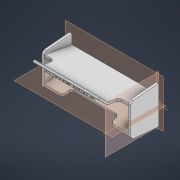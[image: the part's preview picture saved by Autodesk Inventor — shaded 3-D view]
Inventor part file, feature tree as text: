
AUTODESK INVENTOR PART (.ipt)
format: ipt  version: 2021 (Build 250183000, 183)  size: 4,402,176 bytes
history: native  units: mm
features: other x5, extrude x5, sketch x4, chamfer x2, move_body x2, fillet x1, mirror x1
ambient origin geometry x8: Origin, YZ Plane, XZ Plane, XY Plane, X Axis, Y Axis, Z Axis, Center Point
bodies: Solid1 (feature_tree)
feature tree (20):
  other  "Blocks"
  extrude  "Extrusion1"  Depth=35.0mm
  extrude  "Extrusion2"  TaperAngle=0.0deg  [1 undecoded]
  extrude  "Extrusion5"  Depth=2.5mm
  extrude  "Extrusion6"  Depth=2.5mm
  fillet  "Fillet1"  Radius=2.5mm
  mirror  "Mirror1"
  extrude  "Extrusion8"  Depth=2.5mm
  chamfer  "Chamfer1"  Distance=17.453293mm
  chamfer  "Chamfer2"  Distance=17.453293mm
  move_body  "Move Body1"
  move_body  "Move Body2"
  sketch  "Sketch2"  dims[d4=30.0mm d5=35.0mm]
  sketch  "Sketch5"  dims[d6=40.0mm d14=0.0mm]
  sketch  "Sketch8"  dims[d15=2.5mm d16=2.5mm]
  other  "Block1"
  sketch  "Sketch15"  dims[d17=2.5mm d18=2.5mm d19=2.5mm d20=40.0mm d22=17.453293mm d23=17.453293mm d24=45.0mm d25=0.0mm d33=10.0mm d34=25.0mm d35=2.5mm d36=0.0mm d38=10.0mm d39=2.5mm d40=0.0mm d41=2.5mm d43=2.5mm d45=45.0deg d46=10.0mm d47=100.0mm d60=1.5mm d61=0.0mm d62=2.5mm d63=2.0mm d64=45.0deg d65=0.5mm d66=2.0mm d67=45.0deg d68=90.0deg d69=180.0deg]
  other  "lgcc"
  other  "lgcc2"
  other  "lgcc2:1"
note: 1 required parameter value undecoded (feature->parameter linkage not recoverable at this tier; creation-order binding heuristic only, values carry confidence <= 0.55)
